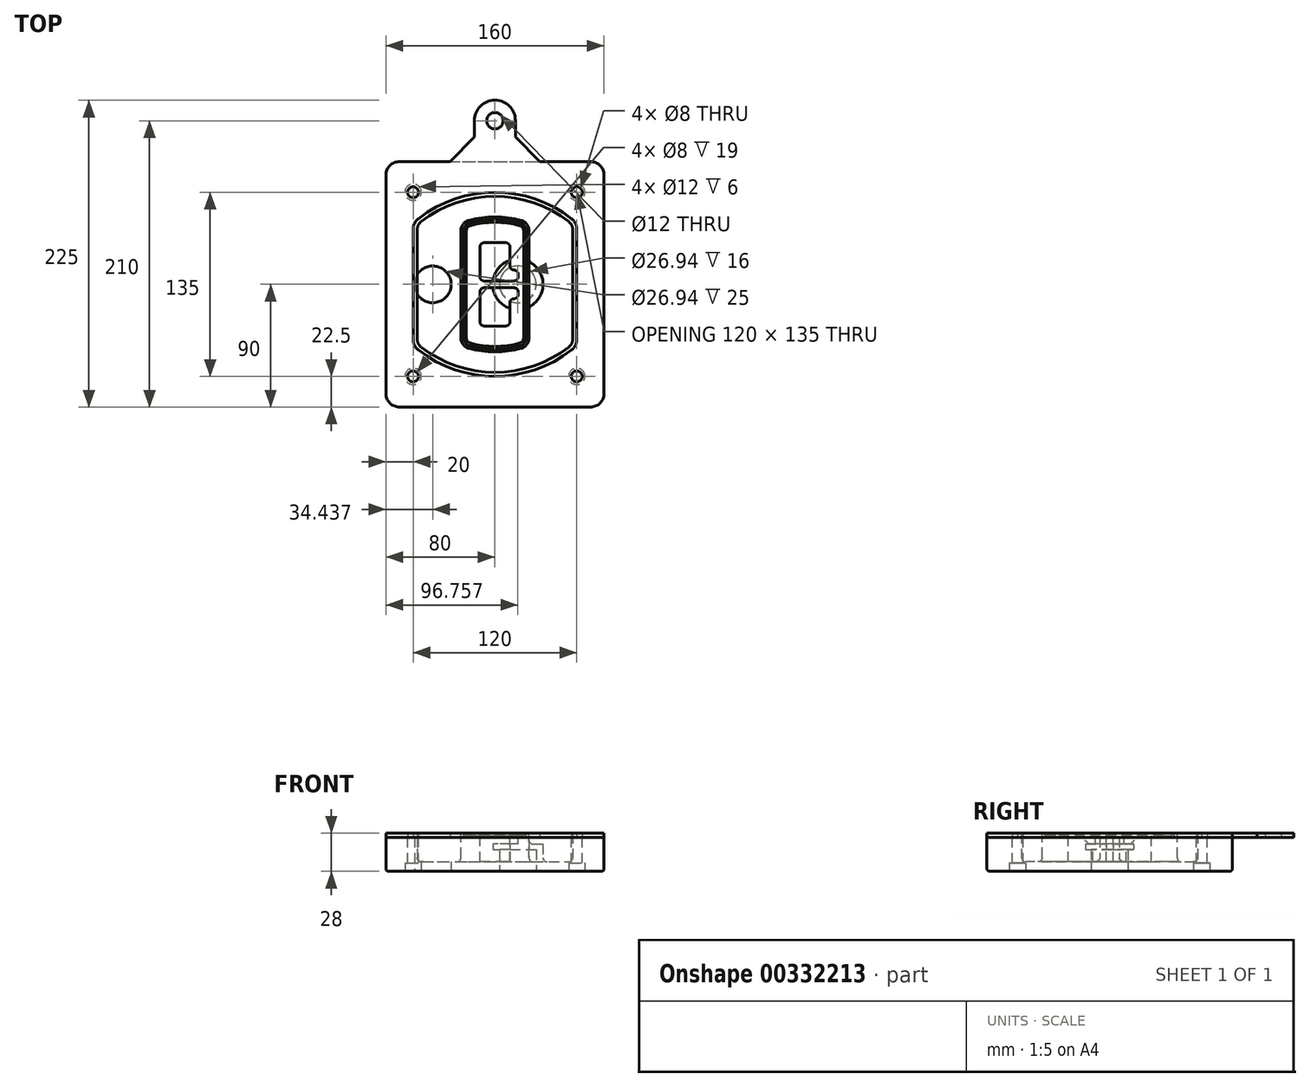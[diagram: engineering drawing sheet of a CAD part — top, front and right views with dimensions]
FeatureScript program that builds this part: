
annotation { "Feature Type Name" : "Feature", "Feature Type Description" : "" }
export const myFeature = defineFeature(function(context is Context, id is Id, definition is map)
    precondition{}
    {
        {
            var Q0;
            Q0=qCreatedBy(makeId("Top.planeOp"),FACE);
            var sketch = newSketch(context, id + "F0", { "sketchPlane" : qUnion([Q0])});
            skPoint(sketch, "E0.rect.middle", {"position": v(0, 0) * mm});
            skLineSegment(sketch, "E1.bottom", {"start": v(-70, -90) * mm, "end": v(70, -90) * mm});
            skLineSegment(sketch, "E1.top", {"start": v(-70, 90) * mm, "end": v(70, 90) * mm});
            skLineSegment(sketch, "E1.left", {"start": v(-80, -80) * mm, "end": v(-80, 80) * mm});
            skLineSegment(sketch, "E1.right", {"start": v(80, -80) * mm, "end": v(80, 80) * mm});
            skLineSegment(sketch, "E2", {"start": v(-80, 90) * mm, "end": v(80, -90) * mm, "construction": true});
            skLineSegment(sketch, "E3", {"start": v(80, 90) * mm, "end": v(-80, -90) * mm, "construction": true});
            skCircle(sketch, "E4", {"center": v(-60, 67.5) * mm, "radius": 4 * mm});
            skCircle(sketch, "E5", {"center": v(60, 67.5) * mm, "radius": 4 * mm});
            skCircle(sketch, "E6", {"center": v(60, -67.5) * mm, "radius": 4 * mm});
            skCircle(sketch, "E7", {"center": v(-60, -67.5) * mm, "radius": 4 * mm});
            skLineSegment(sketch, "E8", {"start": v(-60, 67.5) * mm, "end": v(60, 67.5) * mm, "construction": true});
            skLineSegment(sketch, "E9", {"start": v(60, 67.5) * mm, "end": v(60, -67.5) * mm, "construction": true});
            skLineSegment(sketch, "E10", {"start": v(60, -67.5) * mm, "end": v(-60, -67.5) * mm, "construction": true});
            skLineSegment(sketch, "E11", {"start": v(-60, -67.5) * mm, "end": v(-60, 67.5) * mm, "construction": true});
            skLineSegment(sketch, "E12", {"start": v(-60, 40.3) * mm, "end": v(-60, -40.3) * mm});
            skLineSegment(sketch, "E13", {"start": v(60, 40.3) * mm, "end": v(60, -40.3) * mm});
            skArc(sketch, "E14", {"start": v(56.15, 48.18) * mm, "mid": v(0, 67.5) * mm, "end": v(-56.15, 48.18) * mm});
            skArc(sketch, "E15", {"start": v(-56.15, -48.18) * mm, "mid": v(0, -67.5) * mm, "end": v(56.15, -48.18) * mm});
            skLineSegment(sketch, "E16", {"start": v(-60, 0) * mm, "end": v(60, 0) * mm, "construction": true});
            skPoint(sketch, "E17.visualSharp", {"position": v(-60, -45) * mm});
            skArc(sketch, "E17.filletArc", {"start": v(-60, -40.3) * mm, "mid": v(-58.99, -44.68) * mm, "end": v(-56.15, -48.18) * mm});
            skPoint(sketch, "E18.visualSharp", {"position": v(-60, 45) * mm});
            skArc(sketch, "E18.filletArc", {"start": v(-56.15, 48.18) * mm, "mid": v(-58.99, 44.68) * mm, "end": v(-60, 40.3) * mm});
            skPoint(sketch, "E19.visualSharp", {"position": v(60, 45) * mm});
            skArc(sketch, "E19.filletArc", {"start": v(60, 40.3) * mm, "mid": v(58.99, 44.68) * mm, "end": v(56.15, 48.18) * mm});
            skPoint(sketch, "E20.visualSharp", {"position": v(60, -45) * mm});
            skArc(sketch, "E20.filletArc", {"start": v(56.15, -48.18) * mm, "mid": v(58.99, -44.68) * mm, "end": v(60, -40.3) * mm});
            skPoint(sketch, "E21.visualSharp", {"position": v(-80, 90) * mm});
            skArc(sketch, "E21.filletArc", {"start": v(-70, 90) * mm, "mid": v(-77.07, 87.07) * mm, "end": v(-80, 80) * mm});
            skPoint(sketch, "E22.visualSharp", {"position": v(80, 90) * mm});
            skArc(sketch, "E22.filletArc", {"start": v(80, 80) * mm, "mid": v(77.07, 87.07) * mm, "end": v(70, 90) * mm});
            skPoint(sketch, "E23.visualSharp", {"position": v(80, -90) * mm});
            skArc(sketch, "E23.filletArc", {"start": v(70, -90) * mm, "mid": v(77.07, -87.07) * mm, "end": v(80, -80) * mm});
            skPoint(sketch, "E24.visualSharp", {"position": v(-80, -90) * mm});
            skArc(sketch, "E24.filletArc", {"start": v(-80, -80) * mm, "mid": v(-77.07, -87.07) * mm, "end": v(-70, -90) * mm});
            skArc(sketch, "E25.0", {"start": v(57, 40.3) * mm, "mid": v(56.3, 43.36) * mm, "end": v(54.3, 45.81) * mm});
            skLineSegment(sketch, "E25.1", {"start": v(57, 40.3) * mm, "end": v(57, -40.3) * mm});
            skArc(sketch, "E25.2", {"start": v(54.3, -45.81) * mm, "mid": v(56.3, -43.36) * mm, "end": v(57, -40.3) * mm});
            skArc(sketch, "E25.3", {"start": v(-54.3, -45.81) * mm, "mid": v(0, -64.5) * mm, "end": v(54.3, -45.81) * mm});
            skArc(sketch, "E25.4", {"start": v(-57, -40.3) * mm, "mid": v(-56.3, -43.36) * mm, "end": v(-54.3, -45.81) * mm});
            skArc(sketch, "E25.5", {"start": v(54.3, 45.81) * mm, "mid": v(0, 64.5) * mm, "end": v(-54.3, 45.81) * mm});
            skLineSegment(sketch, "E25.6", {"start": v(-57, 40.3) * mm, "end": v(-57, -40.3) * mm});
            skArc(sketch, "E25.7", {"start": v(-54.3, 45.81) * mm, "mid": v(-56.3, 43.36) * mm, "end": v(-57, 40.3) * mm});
            skArc(sketch, "E26.0", {"start": v(-58.62, 51.33) * mm, "mid": v(-62.58, 46.43) * mm, "end": v(-64, 40.3) * mm});
            skArc(sketch, "E26.1", {"start": v(58.62, 51.33) * mm, "mid": v(0, 71.5) * mm, "end": v(-58.62, 51.33) * mm});
            skArc(sketch, "E26.2", {"start": v(64, 40.3) * mm, "mid": v(62.58, 46.43) * mm, "end": v(58.62, 51.33) * mm});
            skLineSegment(sketch, "E26.3", {"start": v(64, 40.3) * mm, "end": v(64, -40.3) * mm});
            skArc(sketch, "E26.4", {"start": v(58.62, -51.33) * mm, "mid": v(62.58, -46.43) * mm, "end": v(64, -40.3) * mm});
            skLineSegment(sketch, "E26.5", {"start": v(-64, 40.3) * mm, "end": v(-64, -40.3) * mm});
            skArc(sketch, "E26.6", {"start": v(-58.62, -51.33) * mm, "mid": v(0, -71.5) * mm, "end": v(58.62, -51.33) * mm});
            skArc(sketch, "E26.7", {"start": v(-64, -40.3) * mm, "mid": v(-62.58, -46.43) * mm, "end": v(-58.62, -51.33) * mm});
            skSolve(sketch);
        }
        {
            var Q0;
            Q0=makeQuery(id+"F0.imprint","IMPRINT",FACE,{"disambiguationData":[TD([[makeQuery(id+"F0.imprint","IMPRINT",EDGE,{"derivedFrom":sQuery(id+"F0.wireOp",EDGE,"E1.bottom")}),1.0]])]});
            var Q1;
            Q1=makeQuery(id+"F0.imprint","IMPRINT",FACE,{"disambiguationData":[TD([[makeQuery(id+"F0.imprint","IMPRINT",EDGE,{"derivedFrom":sQuery(id+"F0.wireOp",EDGE,"E12")}),1.0]])]});
            var Q2;
            Q2=makeQuery(id+"F0.imprint","IMPRINT",FACE,{"disambiguationData":[TD([[makeQuery(id+"F0.imprint","IMPRINT",EDGE,{"derivedFrom":sQuery(id+"F0.wireOp",EDGE,"E25.0")}),1.0]])]});
            var Q3;
            Q3=makeQuery(id+"F0.imprint","IMPRINT",FACE,{"disambiguationData":[TD([[makeQuery(id+"F0.imprint","IMPRINT",EDGE,{"derivedFrom":sQuery(id+"F0.wireOp",EDGE,"E12")}),-1.0]])]});
            extrude(context, id + "F1", {"entities" : qUnion([Q0, Q1, Q2, Q3]), "oppositeDirection" : true, "depth" : 25 * mm});
        }
        {
            var Q0;
            Q0=makeQuery(id+"F0.imprint","IMPRINT",FACE,{"disambiguationData":[TD([[makeQuery(id+"F0.imprint","IMPRINT",EDGE,{"derivedFrom":sQuery(id+"F0.wireOp",EDGE,"E12")}),1.0]])]});
            extrude(context, id + "F2", {"entities" : qUnion([Q0]), "operationType" : NewBodyOperationType.ADD, "depth" : 3 * mm});
        }
        {
            var Q0;
            Q0=makeQuery(id+"F0.imprint","IMPRINT",FACE,{"disambiguationData":[TD([[makeQuery(id+"F0.imprint","IMPRINT",EDGE,{"derivedFrom":sQuery(id+"F0.wireOp",EDGE,"E25.0")}),1.0]])]});
            extrude(context, id + "F3", {"entities" : qUnion([Q0]), "operationType" : NewBodyOperationType.REMOVE, "oppositeDirection" : true, "depth" : 18 * mm});
        }
        {
            var Q0;
            Q0=makeQuery(id+"F2.opExtrude","CAP_FACE",FACE,{"disambiguationData":[OSD([sQuery(id+"F0.wireOp",EDGE,"E12"),sQuery(id+"F0.wireOp",EDGE,"E13"),sQuery(id+"F0.wireOp",EDGE,"E14"),sQuery(id+"F0.wireOp",EDGE,"E15"),sQuery(id+"F0.wireOp",EDGE,"E17.filletArc"),sQuery(id+"F0.wireOp",EDGE,"E18.filletArc"),sQuery(id+"F0.wireOp",EDGE,"E19.filletArc"),sQuery(id+"F0.wireOp",EDGE,"E20.filletArc"),sQuery(id+"F0.wireOp",EDGE,"E25.0"),sQuery(id+"F0.wireOp",EDGE,"E25.1"),sQuery(id+"F0.wireOp",EDGE,"E25.2"),sQuery(id+"F0.wireOp",EDGE,"E25.3"),sQuery(id+"F0.wireOp",EDGE,"E25.4"),sQuery(id+"F0.wireOp",EDGE,"E25.5"),sQuery(id+"F0.wireOp",EDGE,"E25.6"),sQuery(id+"F0.wireOp",EDGE,"E25.7")])],"isStart":false});
            var sketch = newSketch(context, id + "F4", { "sketchPlane" : qUnion([Q0])});
            skArc(sketch, "E27.0", {"start": v(-19.08, -46.97) * mm, "mid": v(0, -49.5) * mm, "end": v(19.08, -46.97) * mm});
            skArc(sketch, "E28.0", {"start": v(19.08, 46.97) * mm, "mid": v(0, 49.5) * mm, "end": v(-19.08, 46.97) * mm});
            skLineSegment(sketch, "E29", {"start": v(-25, 39.25) * mm, "end": v(-25, -39.25) * mm});
            skLineSegment(sketch, "E30", {"start": v(25, 39.25) * mm, "end": v(25, -39.25) * mm});
            skLineSegment(sketch, "E31", {"start": v(-25, 45.1) * mm, "end": v(25, 45.1) * mm, "construction": true});
            skLineSegment(sketch, "E32", {"start": v(-25, -45.1) * mm, "end": v(25, -45.1) * mm, "construction": true});
            skPoint(sketch, "E33.visualSharp", {"position": v(-25, 45.1) * mm});
            skArc(sketch, "E33.filletArc", {"start": v(-19.08, 46.97) * mm, "mid": v(-23.35, 44.11) * mm, "end": v(-25, 39.25) * mm});
            skPoint(sketch, "E34.visualSharp", {"position": v(25, 45.1) * mm});
            skArc(sketch, "E34.filletArc", {"start": v(25, 39.25) * mm, "mid": v(23.35, 44.11) * mm, "end": v(19.08, 46.97) * mm});
            skPoint(sketch, "E35.visualSharp", {"position": v(25, -45.1) * mm});
            skArc(sketch, "E35.filletArc", {"start": v(19.08, -46.97) * mm, "mid": v(23.35, -44.11) * mm, "end": v(25, -39.25) * mm});
            skPoint(sketch, "E36.visualSharp", {"position": v(-25, -45.1) * mm});
            skArc(sketch, "E36.filletArc", {"start": v(-25, -39.25) * mm, "mid": v(-23.35, -44.11) * mm, "end": v(-19.08, -46.97) * mm});
            skArc(sketch, "E37.0", {"start": v(54.3, 45.81) * mm, "mid": v(0, 64.5) * mm, "end": v(-54.3, 45.81) * mm});
            skArc(sketch, "E37.1", {"start": v(-54.3, 45.81) * mm, "mid": v(-56.3, 43.36) * mm, "end": v(-57, 40.3) * mm});
            skLineSegment(sketch, "E37.2", {"start": v(-57, 40.3) * mm, "end": v(-57, -40.3) * mm});
            skArc(sketch, "E37.3", {"start": v(-57, -40.3) * mm, "mid": v(-56.3, -43.36) * mm, "end": v(-54.3, -45.81) * mm});
            skArc(sketch, "E37.4", {"start": v(-54.3, -45.81) * mm, "mid": v(0, -64.5) * mm, "end": v(54.3, -45.81) * mm});
            skArc(sketch, "E37.5", {"start": v(54.3, -45.81) * mm, "mid": v(56.3, -43.36) * mm, "end": v(57, -40.3) * mm});
            skLineSegment(sketch, "E37.6", {"start": v(57, 40.3) * mm, "end": v(57, -40.3) * mm});
            skArc(sketch, "E37.7", {"start": v(57, 40.3) * mm, "mid": v(56.3, 43.36) * mm, "end": v(54.3, 45.81) * mm});
            skLineSegment(sketch, "E38.0", {"start": v(23, 39.25) * mm, "end": v(23, -39.25) * mm});
            skArc(sketch, "E38.1", {"start": v(18.56, -45.04) * mm, "mid": v(21.76, -42.9) * mm, "end": v(23, -39.25) * mm});
            skArc(sketch, "E38.2", {"start": v(-18.56, -45.04) * mm, "mid": v(0, -47.5) * mm, "end": v(18.56, -45.04) * mm});
            skArc(sketch, "E38.3", {"start": v(-23, -39.25) * mm, "mid": v(-21.76, -42.9) * mm, "end": v(-18.56, -45.04) * mm});
            skLineSegment(sketch, "E38.4", {"start": v(-23, 39.25) * mm, "end": v(-23, -39.25) * mm});
            skArc(sketch, "E38.5", {"start": v(23, 39.25) * mm, "mid": v(21.76, 42.9) * mm, "end": v(18.56, 45.04) * mm});
            skArc(sketch, "E38.6", {"start": v(-18.56, 45.04) * mm, "mid": v(-21.76, 42.9) * mm, "end": v(-23, 39.25) * mm});
            skArc(sketch, "E38.7", {"start": v(18.56, 45.04) * mm, "mid": v(0, 47.5) * mm, "end": v(-18.56, 45.04) * mm});
            skArc(sketch, "E39.0", {"start": v(21, 39.25) * mm, "mid": v(20.18, 41.68) * mm, "end": v(18.04, 43.1) * mm});
            skLineSegment(sketch, "E39.1", {"start": v(21, 39.25) * mm, "end": v(21, -39.25) * mm});
            skArc(sketch, "E39.2", {"start": v(18.04, -43.1) * mm, "mid": v(20.18, -41.68) * mm, "end": v(21, -39.25) * mm});
            skArc(sketch, "E39.3", {"start": v(-18.04, -43.1) * mm, "mid": v(0, -45.5) * mm, "end": v(18.04, -43.1) * mm});
            skArc(sketch, "E39.4", {"start": v(-21, -39.25) * mm, "mid": v(-20.18, -41.68) * mm, "end": v(-18.04, -43.1) * mm});
            skArc(sketch, "E39.5", {"start": v(18.04, 43.1) * mm, "mid": v(0, 45.5) * mm, "end": v(-18.04, 43.1) * mm});
            skLineSegment(sketch, "E39.6", {"start": v(-21, 39.25) * mm, "end": v(-21, -39.25) * mm});
            skArc(sketch, "E39.7", {"start": v(-18.04, 43.1) * mm, "mid": v(-20.18, 41.68) * mm, "end": v(-21, 39.25) * mm});
            skLineSegment(sketch, "E40", {"start": v(-25, 0) * mm, "end": v(25, 0) * mm, "construction": true});
            skLineSegment(sketch, "E41", {"start": v(-11, 5.5) * mm, "end": v(-11, 27.5) * mm});
            skLineSegment(sketch, "E42", {"start": v(-8, 30.5) * mm, "end": v(8, 30.5) * mm});
            skLineSegment(sketch, "E43", {"start": v(11, 27.5) * mm, "end": v(11, 13.5) * mm});
            skLineSegment(sketch, "E44", {"start": v(14, 10.5) * mm, "end": v(14, 10.5) * mm});
            skLineSegment(sketch, "E45", {"start": v(17, 7.5) * mm, "end": v(17, 5.5) * mm});
            skLineSegment(sketch, "E46", {"start": v(14, 2.5) * mm, "end": v(-8, 2.5) * mm});
            skPoint(sketch, "E47.visualSharp", {"position": v(-11, 30.5) * mm});
            skArc(sketch, "E47.filletArc", {"start": v(-8, 30.5) * mm, "mid": v(-10.12, 29.62) * mm, "end": v(-11, 27.5) * mm});
            skPoint(sketch, "E48.visualSharp", {"position": v(11, 30.5) * mm});
            skArc(sketch, "E48.filletArc", {"start": v(11, 27.5) * mm, "mid": v(10.12, 29.62) * mm, "end": v(8, 30.5) * mm});
            skPoint(sketch, "E49.visualSharp", {"position": v(11, 10.5) * mm});
            skArc(sketch, "E49.filletArc", {"start": v(11, 13.5) * mm, "mid": v(11.88, 11.38) * mm, "end": v(14, 10.5) * mm});
            skPoint(sketch, "E50.visualSharp", {"position": v(17, 10.5) * mm});
            skArc(sketch, "E50.filletArc", {"start": v(17, 7.5) * mm, "mid": v(16.12, 9.62) * mm, "end": v(14, 10.5) * mm});
            skPoint(sketch, "E51.visualSharp", {"position": v(17, 2.5) * mm});
            skArc(sketch, "E51.filletArc", {"start": v(14, 2.5) * mm, "mid": v(16.12, 3.38) * mm, "end": v(17, 5.5) * mm});
            skPoint(sketch, "E52.visualSharp", {"position": v(-11, 2.5) * mm});
            skArc(sketch, "E52.filletArc", {"start": v(-11, 5.5) * mm, "mid": v(-10.12, 3.38) * mm, "end": v(-8, 2.5) * mm});
            skLineSegment(sketch, "E53.0.MirrorCS", {"start": v(14, -2.5) * mm, "end": v(-8, -2.5) * mm});
            skArc(sketch, "E54.0.MirrorCS", {"start": v(-11, -5.5) * mm, "mid": v(-10.12, -3.38) * mm, "end": v(-8, -2.5) * mm});
            skLineSegment(sketch, "E55.0.MirrorCS", {"start": v(-11, -5.5) * mm, "end": v(-11, -27.5) * mm});
            skArc(sketch, "E56.0.MirrorCS", {"start": v(-8, -30.5) * mm, "mid": v(-10.12, -29.62) * mm, "end": v(-11, -27.5) * mm});
            skLineSegment(sketch, "E57.0.MirrorCS", {"start": v(-8, -30.5) * mm, "end": v(8, -30.5) * mm});
            skArc(sketch, "E58.0.MirrorCS", {"start": v(11, -27.5) * mm, "mid": v(10.12, -29.62) * mm, "end": v(8, -30.5) * mm});
            skLineSegment(sketch, "E59.0.MirrorCS", {"start": v(11, -27.5) * mm, "end": v(11, -13.5) * mm});
            skArc(sketch, "E60.0.MirrorCS", {"start": v(11, -13.5) * mm, "mid": v(11.88, -11.38) * mm, "end": v(14, -10.5) * mm});
            skArc(sketch, "E61.0.MirrorCS", {"start": v(17, -7.5) * mm, "mid": v(16.12, -9.62) * mm, "end": v(14, -10.5) * mm});
            skLineSegment(sketch, "E62.0.MirrorCS", {"start": v(17, -7.5) * mm, "end": v(17, -5.5) * mm});
            skArc(sketch, "E63.0.MirrorCS", {"start": v(14, -2.5) * mm, "mid": v(16.12, -3.38) * mm, "end": v(17, -5.5) * mm});
            skSolve(sketch);
        }
        {
            var Q0;
            Q0=makeQuery(id+"F4.imprint","IMPRINT",FACE,{"disambiguationData":[TD([[makeQuery(id+"F4.imprint","IMPRINT",EDGE,{"derivedFrom":sQuery(id+"F4.wireOp",EDGE,"E27.0")}),1.0]])]});
            var Q1;
            Q1=makeQuery(id+"F4.imprint","IMPRINT",FACE,{"disambiguationData":[TD([[makeQuery(id+"F4.imprint","IMPRINT",EDGE,{"derivedFrom":sQuery(id+"F4.wireOp",EDGE,"E38.0")}),-1.0]])]});
            var Q2;
            Q2=makeQuery(id+"F4.imprint","IMPRINT",FACE,{"disambiguationData":[TD([[makeQuery(id+"F4.imprint","IMPRINT",EDGE,{"derivedFrom":sQuery(id+"F4.wireOp",EDGE,"E39.0")}),1.0]])]});
            extrude(context, id + "F5", {"entities" : qUnion([Q0, Q1, Q2]), "operationType" : NewBodyOperationType.ADD, "endBound" : BoundingType.UP_TO_NEXT, "oppositeDirection" : true, "depth" : 25 * mm});
        }
        {
            var Q0;
            Q0=makeQuery(id+"F4.imprint","IMPRINT",FACE,{"disambiguationData":[TD([[makeQuery(id+"F4.imprint","IMPRINT",EDGE,{"derivedFrom":sQuery(id+"F4.wireOp",EDGE,"E38.0")}),-1.0]])]});
            extrude(context, id + "F6", {"entities" : qUnion([Q0]), "operationType" : NewBodyOperationType.REMOVE, "oppositeDirection" : true, "depth" : 2 * mm});
        }
        {
            var Q0;
            Q0=makeQuery(id+"F1.opExtrude","CAP_FACE",FACE,{"disambiguationData":[OSD([sQuery(id+"F0.wireOp",EDGE,"E1.bottom"),sQuery(id+"F0.wireOp",EDGE,"E1.top"),sQuery(id+"F0.wireOp",EDGE,"E1.left"),sQuery(id+"F0.wireOp",EDGE,"E1.right"),sQuery(id+"F0.wireOp",EDGE,"E4"),sQuery(id+"F0.wireOp",EDGE,"E5"),sQuery(id+"F0.wireOp",EDGE,"E6"),sQuery(id+"F0.wireOp",EDGE,"E7"),sQuery(id+"F0.wireOp",EDGE,"E21.filletArc"),sQuery(id+"F0.wireOp",EDGE,"E22.filletArc"),sQuery(id+"F0.wireOp",EDGE,"E23.filletArc"),sQuery(id+"F0.wireOp",EDGE,"E24.filletArc")])],"isStart":false});
            var sketch = newSketch(context, id + "F7", { "sketchPlane" : qUnion([Q0])});
            skCircle(sketch, "E64", {"center": v(16.76, 0) * mm, "radius": 13.47 * mm});
            skCircle(sketch, "E65", {"center": v(-45.56, 0) * mm, "radius": 13.47 * mm});
            skLineSegment(sketch, "E66", {"start": v(80, 0) * mm, "end": v(-80, 0) * mm});
            skCircle(sketch, "E67", {"center": v(16.76, 0) * mm, "radius": 18.47 * mm});
            skCircle(sketch, "E68", {"center": v(60, -67.5) * mm, "radius": 6 * mm});
            skCircle(sketch, "E69", {"center": v(-60, -67.5) * mm, "radius": 6 * mm});
            skCircle(sketch, "E70", {"center": v(-60, 67.5) * mm, "radius": 6 * mm});
            skCircle(sketch, "E71", {"center": v(60, 67.5) * mm, "radius": 6 * mm});
            skSolve(sketch);
        }
        {
            var Q0;
            {var subQ1=sQuery(id+"F7.wireOp",EDGE,"E66");var subQ4=sQuery(id+"F7.wireOp",EDGE,"E64");var subQ6=makeQuery(id+"F7.imprint","INTERSECT",VERTEX,{"disambiguationData":[OD(0.0)],"derivedFrom":[subQ4,subQ1]});Q0=makeQuery(id+"F7.imprint","IMPRINT",FACE,{"disambiguationData":[TD([[makeQuery(id+"F7.imprint","IMPRINT",EDGE,{"disambiguationData":[TD([[subQ6,-1.0]])],"derivedFrom":subQ4}),-1.0]])]});}
            var Q1;
            {var subQ0=sQuery(id+"F7.wireOp",EDGE,"E66");var subQ1=sQuery(id+"F7.wireOp",EDGE,"E64");var subQ3=makeQuery(id+"F7.imprint","INTERSECT",VERTEX,{"disambiguationData":[OD(0.0)],"derivedFrom":[subQ1,subQ0]});Q1=makeQuery(id+"F7.imprint","IMPRINT",FACE,{"disambiguationData":[TD([[makeQuery(id+"F7.imprint","IMPRINT",EDGE,{"disambiguationData":[TD([[subQ3,-1.0]])],"derivedFrom":subQ1}),1.0]])]});}
            var Q2;
            {var subQ0=sQuery(id+"F7.wireOp",EDGE,"E66");var subQ1=sQuery(id+"F7.wireOp",EDGE,"E64");var subQ3=makeQuery(id+"F7.imprint","INTERSECT",VERTEX,{"disambiguationData":[OD(0.0)],"derivedFrom":[subQ1,subQ0]});Q2=makeQuery(id+"F7.imprint","IMPRINT",FACE,{"disambiguationData":[TD([[makeQuery(id+"F7.imprint","IMPRINT",EDGE,{"disambiguationData":[TD([[subQ3,1.0]])],"derivedFrom":subQ1}),1.0]])]});}
            var Q3;
            {var subQ1=sQuery(id+"F7.wireOp",EDGE,"E66");var subQ4=sQuery(id+"F7.wireOp",EDGE,"E64");var subQ6=makeQuery(id+"F7.imprint","INTERSECT",VERTEX,{"disambiguationData":[OD(0.0)],"derivedFrom":[subQ4,subQ1]});Q3=makeQuery(id+"F7.imprint","IMPRINT",FACE,{"disambiguationData":[TD([[makeQuery(id+"F7.imprint","IMPRINT",EDGE,{"disambiguationData":[TD([[subQ6,1.0]])],"derivedFrom":subQ4}),-1.0]])]});}
            extrude(context, id + "F8", {"entities" : qUnion([Q0, Q1, Q2, Q3]), "operationType" : NewBodyOperationType.ADD, "oppositeDirection" : true, "depth" : 20 * mm});
        }
        {
            var Q0;
            {var subQ0=sQuery(id+"F7.wireOp",EDGE,"E66");var subQ1=sQuery(id+"F7.wireOp",EDGE,"E64");var subQ3=makeQuery(id+"F7.imprint","INTERSECT",VERTEX,{"disambiguationData":[OD(0.0)],"derivedFrom":[subQ1,subQ0]});Q0=makeQuery(id+"F7.imprint","IMPRINT",FACE,{"disambiguationData":[TD([[makeQuery(id+"F7.imprint","IMPRINT",EDGE,{"disambiguationData":[TD([[subQ3,-1.0]])],"derivedFrom":subQ1}),1.0]])]});}
            var Q1;
            {var subQ0=sQuery(id+"F7.wireOp",EDGE,"E66");var subQ1=sQuery(id+"F7.wireOp",EDGE,"E64");var subQ3=makeQuery(id+"F7.imprint","INTERSECT",VERTEX,{"disambiguationData":[OD(0.0)],"derivedFrom":[subQ1,subQ0]});Q1=makeQuery(id+"F7.imprint","IMPRINT",FACE,{"disambiguationData":[TD([[makeQuery(id+"F7.imprint","IMPRINT",EDGE,{"disambiguationData":[TD([[subQ3,1.0]])],"derivedFrom":subQ1}),1.0]])]});}
            extrude(context, id + "F9", {"entities" : qUnion([Q0, Q1]), "operationType" : NewBodyOperationType.REMOVE, "oppositeDirection" : true, "depth" : 16 * mm});
        }
        {
            var Q0;
            {var subQ0=sQuery(id+"F7.wireOp",EDGE,"E66");var subQ1=sQuery(id+"F7.wireOp",EDGE,"E65");var subQ3=makeQuery(id+"F7.imprint","INTERSECT",VERTEX,{"disambiguationData":[OD(0.0)],"derivedFrom":[subQ1,subQ0]});Q0=makeQuery(id+"F7.imprint","IMPRINT",FACE,{"disambiguationData":[TD([[makeQuery(id+"F7.imprint","IMPRINT",EDGE,{"disambiguationData":[TD([[subQ3,-1.0]])],"derivedFrom":subQ1}),1.0]])]});}
            var Q1;
            {var subQ0=sQuery(id+"F7.wireOp",EDGE,"E66");var subQ1=sQuery(id+"F7.wireOp",EDGE,"E65");var subQ3=makeQuery(id+"F7.imprint","INTERSECT",VERTEX,{"disambiguationData":[OD(0.0)],"derivedFrom":[subQ1,subQ0]});Q1=makeQuery(id+"F7.imprint","IMPRINT",FACE,{"disambiguationData":[TD([[makeQuery(id+"F7.imprint","IMPRINT",EDGE,{"disambiguationData":[TD([[subQ3,1.0]])],"derivedFrom":subQ1}),1.0]])]});}
            extrude(context, id + "F10", {"entities" : qUnion([Q0, Q1]), "operationType" : NewBodyOperationType.REMOVE, "oppositeDirection" : true, "depth" : 25 * mm});
        }
        {
            var Q0;
            Q0=makeQuery(id+"F7.imprint","IMPRINT",FACE,{"disambiguationData":[TD([[makeQuery(id+"F7.imprint","IMPRINT",EDGE,{"derivedFrom":sQuery(id+"F7.wireOp",EDGE,"E68")}),1.0]])]});
            var Q1;
            Q1=makeQuery(id+"F7.imprint","IMPRINT",FACE,{"disambiguationData":[TD([[makeQuery(id+"F7.imprint","IMPRINT",EDGE,{"derivedFrom":makeQuery(id+"F1.opExtrude","CAP_EDGE",EDGE,{"disambiguationData":[OSD([sQuery(id+"F0.wireOp",EDGE,"E5")])],"isStart":false})}),-1.0]])]});
            var Q2;
            Q2=makeQuery(id+"F7.imprint","IMPRINT",FACE,{"disambiguationData":[TD([[makeQuery(id+"F7.imprint","IMPRINT",EDGE,{"derivedFrom":sQuery(id+"F7.wireOp",EDGE,"E69")}),1.0]])]});
            var Q3;
            Q3=makeQuery(id+"F7.imprint","IMPRINT",FACE,{"disambiguationData":[TD([[makeQuery(id+"F7.imprint","IMPRINT",EDGE,{"derivedFrom":makeQuery(id+"F1.opExtrude","CAP_EDGE",EDGE,{"disambiguationData":[OSD([sQuery(id+"F0.wireOp",EDGE,"E4")])],"isStart":false})}),-1.0]])]});
            var Q4;
            Q4=makeQuery(id+"F7.imprint","IMPRINT",FACE,{"disambiguationData":[TD([[makeQuery(id+"F7.imprint","IMPRINT",EDGE,{"derivedFrom":sQuery(id+"F7.wireOp",EDGE,"E70")}),1.0]])]});
            var Q5;
            Q5=makeQuery(id+"F7.imprint","IMPRINT",FACE,{"disambiguationData":[TD([[makeQuery(id+"F7.imprint","IMPRINT",EDGE,{"derivedFrom":makeQuery(id+"F1.opExtrude","CAP_EDGE",EDGE,{"disambiguationData":[OSD([sQuery(id+"F0.wireOp",EDGE,"E7")])],"isStart":false})}),-1.0]])]});
            var Q6;
            Q6=makeQuery(id+"F7.imprint","IMPRINT",FACE,{"disambiguationData":[TD([[makeQuery(id+"F7.imprint","IMPRINT",EDGE,{"derivedFrom":sQuery(id+"F7.wireOp",EDGE,"E71")}),1.0]])]});
            var Q7;
            Q7=makeQuery(id+"F7.imprint","IMPRINT",FACE,{"disambiguationData":[TD([[makeQuery(id+"F7.imprint","IMPRINT",EDGE,{"derivedFrom":makeQuery(id+"F1.opExtrude","CAP_EDGE",EDGE,{"disambiguationData":[OSD([sQuery(id+"F0.wireOp",EDGE,"E6")])],"isStart":false})}),-1.0]])]});
            extrude(context, id + "F11", {"entities" : qUnion([Q0, Q1, Q2, Q3, Q4, Q5, Q6, Q7]), "operationType" : NewBodyOperationType.REMOVE, "oppositeDirection" : true, "depth" : 6 * mm});
        }
        {
            var Q0;
            Q0=makeQuery(id+"F9.boolean.opBoolean","COPY",FACE,{"derivedFrom":makeQuery(id+"F9.opExtrude","CAP_FACE",FACE,{"disambiguationData":[OSD([sQuery(id+"F7.wireOp",EDGE,"E64")])],"isStart":false})});
            var sketch = newSketch(context, id + "F12", { "sketchPlane" : qUnion([Q0])});
            skArc(sketch, "E72.0", {"start": v(11, 17.55) * mm, "mid": v(2.57, 11.82) * mm, "end": v(-1.54, 2.5) * mm});
            skArc(sketch, "E72.1", {"start": v(-1.54, -2.5) * mm, "mid": v(2.57, -11.82) * mm, "end": v(11, -17.55) * mm});
            skLineSegment(sketch, "E73", {"start": v(-1.54, -2.5) * mm, "end": v(14, -2.5) * mm});
            skLineSegment(sketch, "E74.0", {"start": v(14, 2.5) * mm, "end": v(-1.54, 2.5) * mm});
            skArc(sketch, "E74.1", {"start": v(14, 2.5) * mm, "mid": v(16.12, 3.38) * mm, "end": v(17, 5.5) * mm});
            skLineSegment(sketch, "E74.2", {"start": v(17, 7.5) * mm, "end": v(17, 5.5) * mm});
            skArc(sketch, "E74.3", {"start": v(17, 7.5) * mm, "mid": v(16.12, 9.62) * mm, "end": v(14, 10.5) * mm});
            skArc(sketch, "E74.4", {"start": v(11, 13.5) * mm, "mid": v(11.88, 11.38) * mm, "end": v(14, 10.5) * mm});
            skLineSegment(sketch, "E74.5", {"start": v(11, 17.55) * mm, "end": v(11, 13.5) * mm});
            skLineSegment(sketch, "E74.7", {"start": v(14, -2.5) * mm, "end": v(-1.54, -2.5) * mm});
            skArc(sketch, "E74.8", {"start": v(14, -2.5) * mm, "mid": v(16.12, -3.38) * mm, "end": v(17, -5.5) * mm});
            skLineSegment(sketch, "E74.9", {"start": v(17, -7.5) * mm, "end": v(17, -5.5) * mm});
            skArc(sketch, "E74.10", {"start": v(17, -7.5) * mm, "mid": v(16.12, -9.62) * mm, "end": v(14, -10.5) * mm});
            skArc(sketch, "E74.11", {"start": v(11, -13.5) * mm, "mid": v(11.88, -11.38) * mm, "end": v(14, -10.5) * mm});
            skLineSegment(sketch, "E74.12", {"start": v(11, -17.55) * mm, "end": v(11, -13.5) * mm});
            skPoint(sketch, "E75.orphan", {"position": v(11, -27.5) * mm});
            skPoint(sketch, "E76.orphan", {"position": v(-8, -2.5) * mm});
            skPoint(sketch, "E77.orphan", {"position": v(-8, 2.5) * mm});
            skPoint(sketch, "E78.orphan", {"position": v(11, 27.5) * mm});
            skSolve(sketch);
        }
        {
            var Q0;
            {var subQ7=sQuery(id+"F12.wireOp",EDGE,"E72.0");var subQ14=sQuery(id+"F12.wireOp",EDGE,"E72.1");var subQ16=sQuery(id+"F12.wireOp",EDGE,"E74.1");var subQ18=sQuery(id+"F12.wireOp",EDGE,"E74.8");Q0=qUnion([makeQuery(id+"F12.imprint","IMPRINT",FACE,{"disambiguationData":[TD([[makeQuery(id+"F12.imprint","IMPRINT",EDGE,{"derivedFrom":subQ7}),1.0]])]}),makeQuery(id+"F12.imprint","IMPRINT",FACE,{"disambiguationData":[TD([[makeQuery(id+"F12.imprint","IMPRINT",EDGE,{"derivedFrom":subQ14}),1.0]])]}),makeQuery(id+"F12.imprint","IMPRINT",FACE,{"disambiguationData":[TD([[makeQuery(id+"F12.imprint","IMPRINT",EDGE,{"derivedFrom":subQ16}),1.0]])]}),makeQuery(id+"F12.imprint","IMPRINT",FACE,{"disambiguationData":[TD([[makeQuery(id+"F12.imprint","IMPRINT",EDGE,{"derivedFrom":subQ18}),-1.0]])]})]);}
            var Q1;
            Q1=makeQuery(id+"F5.boolean.opBoolean","SPLIT",FACE,{"disambiguationData":[TD([makeQuery(id+"F5.opExtrude","SWEPT_FACE",FACE,{"disambiguationData":[OSD([sQuery(id+"F4.wireOp",EDGE,"E41")])]})])],"derivedFrom":makeQuery(id+"F3.boolean.opBoolean","COPY",FACE,{"derivedFrom":makeQuery(id+"F3.opExtrude","CAP_FACE",FACE,{"disambiguationData":[OSD([sQuery(id+"F0.wireOp",EDGE,"E25.0"),sQuery(id+"F0.wireOp",EDGE,"E25.1"),sQuery(id+"F0.wireOp",EDGE,"E25.2"),sQuery(id+"F0.wireOp",EDGE,"E25.3"),sQuery(id+"F0.wireOp",EDGE,"E25.4"),sQuery(id+"F0.wireOp",EDGE,"E25.5"),sQuery(id+"F0.wireOp",EDGE,"E25.6"),sQuery(id+"F0.wireOp",EDGE,"E25.7")])],"isStart":false})})});
            extrude(context, id + "F13", {"entities" : qUnion([Q0]), "operationType" : NewBodyOperationType.REMOVE, "endBound" : BoundingType.UP_TO_SURFACE, "endBoundEntityFace" : qUnion([Q1]), "depth" : 25 * mm});
        }
        {
            var Q0;
            Q0=makeQuery(id+"F3.boolean.opBoolean","COPY",EDGE,{"derivedFrom":makeQuery(id+"F3.opExtrude","CAP_EDGE",EDGE,{"disambiguationData":[OSD([sQuery(id+"F0.wireOp",EDGE,"E25.6")])],"isStart":false})});
            var Q1;
            Q1=makeQuery(id+"F8.boolean.opBoolean","INTERSECT",EDGE,{"derivedFrom":[makeQuery(id+"F5.opExtrude","SWEPT_FACE",FACE,{"disambiguationData":[OSD([sQuery(id+"F4.wireOp",EDGE,"E30")])]}),makeQuery(id+"F8.opExtrude","CAP_FACE",FACE,{"disambiguationData":[OSD([sQuery(id+"F7.wireOp",EDGE,"E67")])],"isStart":false})]});
            var Q2;
            Q2=makeQuery(id+"F8.boolean.opBoolean","INTERSECT",EDGE,{"disambiguationData":[OD(1.0)],"derivedFrom":[makeQuery(id+"F5.opExtrude","SWEPT_FACE",FACE,{"disambiguationData":[OSD([sQuery(id+"F4.wireOp",EDGE,"E30")])]}),makeQuery(id+"F8.opExtrude","SWEPT_FACE",FACE,{"disambiguationData":[OSD([sQuery(id+"F7.wireOp",EDGE,"E67")])]})]});
            var Q3;
            {var subQ0=sQuery(id+"F4.wireOp",EDGE,"E30");Q3=makeQuery(id+"F8.boolean.opBoolean","SPLIT",EDGE,{"disambiguationData":[TD([makeQuery(id+"F5.opExtrude","SWEPT_FACE",FACE,{"disambiguationData":[OSD([sQuery(id+"F4.wireOp",EDGE,"E35.filletArc")])]})])],"derivedFrom":makeQuery(id+"F5.opExtrude","CAP_EDGE",EDGE,{"disambiguationData":[OSD([subQ0])],"isStart":false})});}
            var Q4;
            {var subQ0=sQuery(id+"F0.wireOp",EDGE,"E25.7");var subQ1=sQuery(id+"F0.wireOp",EDGE,"E25.1");var subQ2=sQuery(id+"F0.wireOp",EDGE,"E25.6");var subQ3=sQuery(id+"F0.wireOp",EDGE,"E25.5");var subQ4=sQuery(id+"F0.wireOp",EDGE,"E25.4");var subQ5=sQuery(id+"F0.wireOp",EDGE,"E25.0");var subQ6=sQuery(id+"F0.wireOp",EDGE,"E25.2");var subQ7=sQuery(id+"F0.wireOp",EDGE,"E25.3");Q4=makeQuery(id+"F8.boolean.opBoolean","INTERSECT",EDGE,{"derivedFrom":[makeQuery(id+"F5.boolean.opBoolean","SPLIT",FACE,{"disambiguationData":[TD([makeQuery(id+"F2.opExtrude","SWEPT_FACE",FACE,{"disambiguationData":[OSD([subQ5])]})])],"derivedFrom":makeQuery(id+"F3.boolean.opBoolean","COPY",FACE,{"derivedFrom":makeQuery(id+"F3.opExtrude","CAP_FACE",FACE,{"disambiguationData":[OSD([subQ5,subQ1,subQ6,subQ7,subQ4,subQ3,subQ2,subQ0])],"isStart":false})})}),makeQuery(id+"F8.opExtrude","SWEPT_FACE",FACE,{"disambiguationData":[OSD([sQuery(id+"F7.wireOp",EDGE,"E67")])]})]});}
            var Q5;
            Q5=makeQuery(id+"F8.boolean.opBoolean","INTERSECT",EDGE,{"disambiguationData":[OD(0.0)],"derivedFrom":[makeQuery(id+"F5.opExtrude","SWEPT_FACE",FACE,{"disambiguationData":[OSD([sQuery(id+"F4.wireOp",EDGE,"E30")])]}),makeQuery(id+"F8.opExtrude","SWEPT_FACE",FACE,{"disambiguationData":[OSD([sQuery(id+"F7.wireOp",EDGE,"E67")])]})]});
            fillet(context, id + "F14", {"entities" : qUnion([Q0, Q1, Q2, Q3, Q4, Q5]), "radius" : 3 * mm, "tangentPropagation" : true, "allowEdgeOverflow" : false});
        }
        {
            var Q0;
            Q0=makeQuery(id+"F1.opExtrude","CAP_EDGE",EDGE,{"disambiguationData":[OSD([sQuery(id+"F0.wireOp",EDGE,"E1.bottom")])],"isStart":false});
            fillet(context, id + "F15", {"entities" : qUnion([Q0]), "radius" : 2 * mm, "tangentPropagation" : true, "allowEdgeOverflow" : false});
        }
        {
            var Q0;
            {var subQ0=sQuery(id+"F0.wireOp",EDGE,"E21.filletArc");var subQ1=sQuery(id+"F0.wireOp",EDGE,"E7");var subQ2=sQuery(id+"F0.wireOp",EDGE,"E6");var subQ3=sQuery(id+"F0.wireOp",EDGE,"E5");var subQ4=sQuery(id+"F0.wireOp",EDGE,"E4");var subQ5=sQuery(id+"F0.wireOp",EDGE,"E22.filletArc");var subQ6=sQuery(id+"F0.wireOp",EDGE,"E1.bottom");var subQ7=sQuery(id+"F0.wireOp",EDGE,"E1.right");var subQ8=sQuery(id+"F0.wireOp",EDGE,"E1.top");var subQ9=sQuery(id+"F0.wireOp",EDGE,"E1.left");var subQ10=sQuery(id+"F0.wireOp",EDGE,"E23.filletArc");var subQ11=sQuery(id+"F0.wireOp",EDGE,"E24.filletArc");Q0=makeQuery(id+"F2.boolean.opBoolean","SPLIT",FACE,{"disambiguationData":[TD([makeQuery(id+"F1.opExtrude","SWEPT_FACE",FACE,{"disambiguationData":[OSD([subQ6])]})])],"derivedFrom":makeQuery(id+"F1.opExtrude","CAP_FACE",FACE,{"disambiguationData":[OSD([subQ6,subQ8,subQ9,subQ7,subQ4,subQ3,subQ2,subQ1,subQ0,subQ5,subQ10,subQ11])],"isStart":true})});}
            var sketch = newSketch(context, id + "F16", { "sketchPlane" : qUnion([Q0])});
            skLineSegment(sketch, "E79", {"start": v(0, 90) * mm, "end": v(0, 120) * mm, "construction": true});
            skLineSegment(sketch, "E80", {"start": v(33, 90) * mm, "end": v(15, 108) * mm});
            skLineSegment(sketch, "E81", {"start": v(15, 108) * mm, "end": v(15, 120) * mm});
            skLineSegment(sketch, "E82.MirrorCS", {"start": v(-33, 90) * mm, "end": v(-15, 108) * mm});
            skLineSegment(sketch, "E83.MirrorCS", {"start": v(-15, 108) * mm, "end": v(-15, 120) * mm});
            skArc(sketch, "E84", {"start": v(15, 120) * mm, "mid": v(0, 135) * mm, "end": v(-15, 120) * mm});
            skCircle(sketch, "E85", {"center": v(0, 120) * mm, "radius": 6 * mm});
            skLineSegment(sketch, "E86", {"start": v(-80, 0) * mm, "end": v(80, 0) * mm, "construction": true});
            skArc(sketch, "E87.MirrorCS", {"start": v(15, -120) * mm, "mid": v(0, -135) * mm, "end": v(-15, -120) * mm});
            skLineSegment(sketch, "E88.MirrorCS", {"start": v(-15, -108) * mm, "end": v(-15, -120) * mm});
            skCircle(sketch, "E89.MirrorC", {"center": v(0, -120) * mm, "radius": 6 * mm});
            skLineSegment(sketch, "E90.MirrorCS", {"start": v(15, -108) * mm, "end": v(15, -120) * mm});
            skLineSegment(sketch, "E91.MirrorCS", {"start": v(0, -90) * mm, "end": v(0, -120) * mm, "construction": true});
            skLineSegment(sketch, "E92.MirrorCS", {"start": v(33, -90) * mm, "end": v(15, -108) * mm});
            skLineSegment(sketch, "E93.MirrorCS", {"start": v(-33, -90) * mm, "end": v(-15, -108) * mm});
            skSolve(sketch);
        }
        {
            var Q0;
            {var subQ1=sQuery(id+"F16.wireOp",EDGE,"E80");Q0=makeQuery(id+"F16.imprint","IMPRINT",FACE,{"disambiguationData":[TD([[makeQuery(id+"F16.imprint","IMPRINT",EDGE,{"derivedFrom":subQ1}),1.0]])]});}
            var Q1;
            Q1=makeQuery(id+"F16.imprint","IMPRINT",FACE,{"disambiguationData":[TD([[makeQuery(id+"F16.imprint","IMPRINT",EDGE,{"derivedFrom":sQuery(id+"F16.wireOp",EDGE,"E87.MirrorCS")}),-1.0]])]});
            var Q2;
            Q2=makeQuery(id+"F16.imprint","IMPRINT",FACE,{"disambiguationData":[TD([[makeQuery(id+"F16.imprint","IMPRINT",EDGE,{"derivedFrom":makeQuery(id+"F1.opExtrude","CAP_EDGE",EDGE,{"disambiguationData":[OSD([sQuery(id+"F0.wireOp",EDGE,"E1.left")])],"isStart":true})}),-1.0]])]});
            var Q3;
            Q3=makeQuery(id+"F2.opExtrude","CAP_FACE",FACE,{"disambiguationData":[OSD([sQuery(id+"F0.wireOp",EDGE,"E12"),sQuery(id+"F0.wireOp",EDGE,"E13"),sQuery(id+"F0.wireOp",EDGE,"E14"),sQuery(id+"F0.wireOp",EDGE,"E15"),sQuery(id+"F0.wireOp",EDGE,"E17.filletArc"),sQuery(id+"F0.wireOp",EDGE,"E18.filletArc"),sQuery(id+"F0.wireOp",EDGE,"E19.filletArc"),sQuery(id+"F0.wireOp",EDGE,"E20.filletArc"),sQuery(id+"F0.wireOp",EDGE,"E25.0"),sQuery(id+"F0.wireOp",EDGE,"E25.1"),sQuery(id+"F0.wireOp",EDGE,"E25.2"),sQuery(id+"F0.wireOp",EDGE,"E25.3"),sQuery(id+"F0.wireOp",EDGE,"E25.4"),sQuery(id+"F0.wireOp",EDGE,"E25.5"),sQuery(id+"F0.wireOp",EDGE,"E25.6"),sQuery(id+"F0.wireOp",EDGE,"E25.7")])],"isStart":false});
            extrude(context, id + "F17", {"entities" : qUnion([Q0, Q1, Q2]), "endBound" : BoundingType.UP_TO_SURFACE, "endBoundEntityFace" : qUnion([Q3]), "depth" : 25 * mm});
        }
    });
